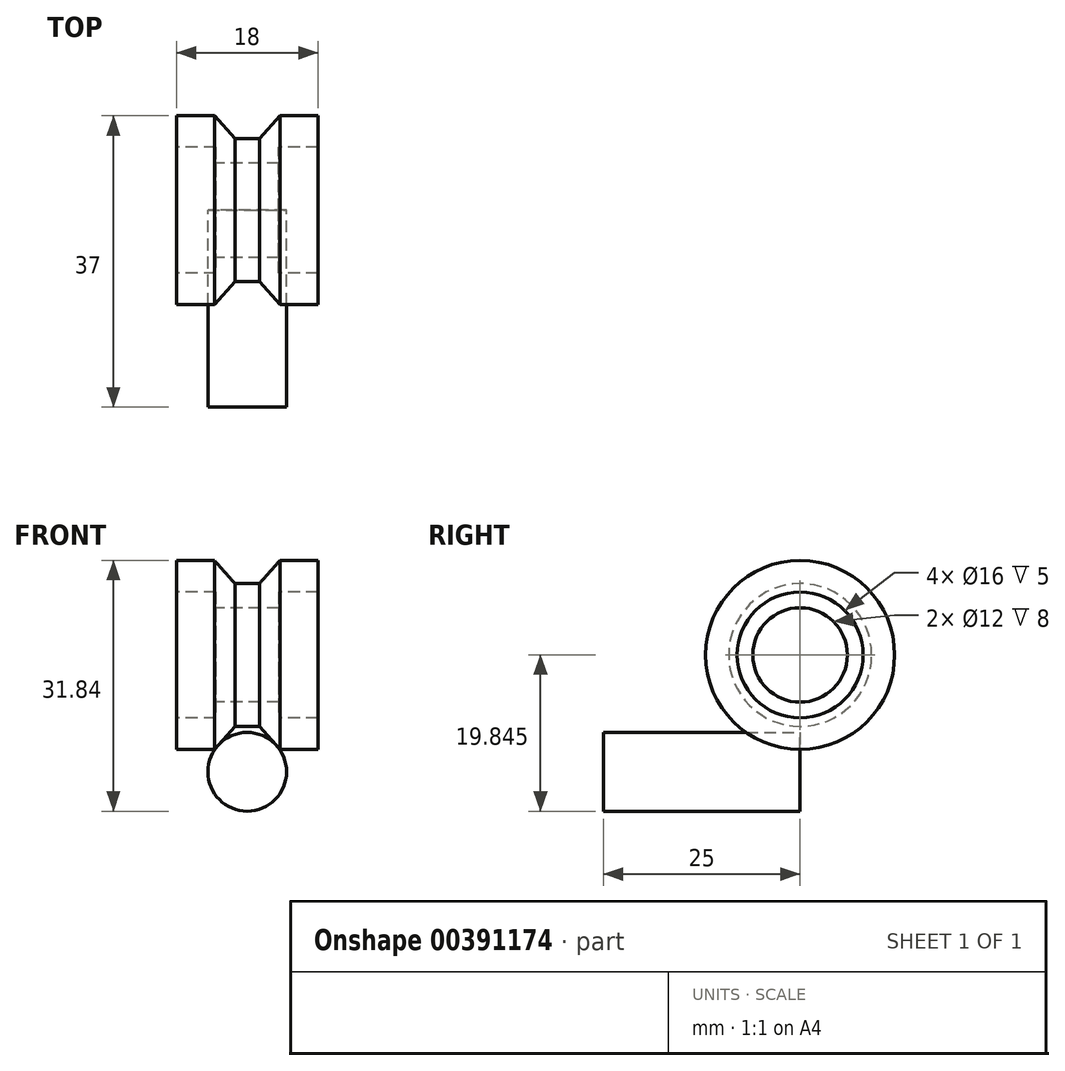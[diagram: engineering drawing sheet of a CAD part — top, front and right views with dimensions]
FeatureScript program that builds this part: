
annotation { "Feature Type Name" : "Feature", "Feature Type Description" : "" }
export const myFeature = defineFeature(function(context is Context, id is Id, definition is map)
    precondition{}
    {
        {
            var Q0;
            Q0=qCreatedBy(makeId("Front.planeOp"),FACE);
            var sketch = newSketch(context, id + "F0", { "sketchPlane" : qUnion([Q0])});
            skCircle(sketch, "E0", {"center": v(0, 0) * mm, "radius": 5 * mm});
            skSolve(sketch);
        }
        {
            var Q0;
            Q0=makeQuery(id+"F0.imprint","IMPRINT",FACE,{"disambiguationData":[TD([[makeQuery(id+"F0.imprint","IMPRINT",EDGE,{"derivedFrom":sQuery(id+"F0.wireOp",EDGE,"E0")}),1.0]])]});
            extrude(context, id + "F1", {"entities" : qUnion([Q0]), "depth" : 25 * mm});
        }
        {
            var Q0;
            Q0=qCreatedBy(makeId("Front.planeOp"),FACE);
            var sketch = newSketch(context, id + "F2", { "sketchPlane" : qUnion([Q0])});
            skLineSegment(sketch, "E1", {"start": v(-4.16, 2.84) * mm, "end": v(-1.56, 5.77) * mm});
            skPoint(sketch, "E2.startSnap0", {"position": v(-3.54, 3.54) * mm});
            skLineSegment(sketch, "E3", {"start": v(-9, 6.84) * mm, "end": v(-9, 2.84) * mm});
            skLineSegment(sketch, "E4", {"start": v(-4.16, 2.84) * mm, "end": v(-9, 2.84) * mm});
            skLineSegment(sketch, "E5.MirrorCS", {"start": v(9, 6.84) * mm, "end": v(9, 2.84) * mm});
            skLineSegment(sketch, "E6.MirrorCS", {"start": v(4.16, 2.84) * mm, "end": v(9, 2.84) * mm});
            skLineSegment(sketch, "E7.MirrorCS", {"start": v(4.16, 2.84) * mm, "end": v(1.56, 5.77) * mm});
            skPoint(sketch, "E8.MirrorP", {"position": v(3.54, 3.54) * mm});
            skLineSegment(sketch, "E9", {"start": v(-9, 6.84) * mm, "end": v(-4, 6.84) * mm});
            skLineSegment(sketch, "E10", {"start": v(9, 6.84) * mm, "end": v(4, 6.84) * mm});
            skLineSegment(sketch, "E11", {"start": v(4, 6.84) * mm, "end": v(4, 8.84) * mm});
            skLineSegment(sketch, "E12", {"start": v(-4, 6.84) * mm, "end": v(-4, 8.84) * mm});
            skLineSegment(sketch, "E13", {"start": v(-4, 14.84) * mm, "end": v(4, 14.84) * mm, "construction": true});
            skLineSegment(sketch, "E14", {"start": v(-1.56, 5.77) * mm, "end": v(1.56, 5.77) * mm});
            skPoint(sketch, "E15.orphan", {"position": v(0, 7.54) * mm});
            skLineSegment(sketch, "E16", {"start": v(-4, 8.84) * mm, "end": v(4, 8.84) * mm});
            skPoint(sketch, "E17.orphan", {"position": v(-4, 14.84) * mm});
            skPoint(sketch, "E18.orphan", {"position": v(4, 14.84) * mm});
            skPoint(sketch, "E19.MirrorP", {"position": v(0, 22.15) * mm});
            skLineSegment(sketch, "E20.MirrorCS", {"start": v(4, 22.84) * mm, "end": v(4, 20.84) * mm});
            skLineSegment(sketch, "E21.MirrorCS", {"start": v(-4, 22.84) * mm, "end": v(-4, 20.84) * mm});
            skPoint(sketch, "E22.MirrorP", {"position": v(3.54, 26.15) * mm});
            skLineSegment(sketch, "E23.MirrorCS", {"start": v(9, 22.84) * mm, "end": v(4, 22.84) * mm});
            skPoint(sketch, "E24.MirrorP", {"position": v(-3.54, 26.15) * mm});
            skLineSegment(sketch, "E25.MirrorCS", {"start": v(9, 22.84) * mm, "end": v(9, 26.84) * mm});
            skLineSegment(sketch, "E26.MirrorCS", {"start": v(4.16, 26.84) * mm, "end": v(9, 26.84) * mm});
            skLineSegment(sketch, "E27.MirrorCS", {"start": v(-9, 22.84) * mm, "end": v(-4, 22.84) * mm});
            skLineSegment(sketch, "E28.MirrorCS", {"start": v(4.16, 26.84) * mm, "end": v(1.56, 23.92) * mm});
            skLineSegment(sketch, "E29.MirrorCS", {"start": v(-4, 20.84) * mm, "end": v(4, 20.84) * mm});
            skLineSegment(sketch, "E30.MirrorCS", {"start": v(-9, 22.84) * mm, "end": v(-9, 26.84) * mm});
            skLineSegment(sketch, "E31.MirrorCS", {"start": v(-1.56, 23.92) * mm, "end": v(1.56, 23.92) * mm});
            skLineSegment(sketch, "E32.MirrorCS", {"start": v(-4.16, 26.84) * mm, "end": v(-9, 26.84) * mm});
            skLineSegment(sketch, "E33.MirrorCS", {"start": v(-4.16, 26.84) * mm, "end": v(-1.56, 23.92) * mm});
            skLineSegment(sketch, "E34", {"start": v(-4, 20.84) * mm, "end": v(-4, 8.84) * mm});
            skLineSegment(sketch, "E35", {"start": v(3.97, 20.67) * mm, "end": v(4, 8.84) * mm});
            skSolve(sketch);
        }
        {
            var Q0;
            Q0=makeQuery(id+"F2.imprint","IMPRINT",FACE,{"disambiguationData":[TD([[makeQuery(id+"F2.imprint","IMPRINT",EDGE,{"derivedFrom":sQuery(id+"F2.wireOp",EDGE,"E20.MirrorCS")}),-1.0]])]});
            var Q1;
            Q1=makeQuery(id+"F2.imprint","IMPRINT",FACE,{"disambiguationData":[TD([[makeQuery(id+"F2.imprint","IMPRINT",EDGE,{"derivedFrom":sQuery(id+"F2.wireOp",EDGE,"E1")}),1.0]])]});
            var Q2;
            Q2=sQuery(id+"F2.wireOp",EDGE,"E13");
            revolve(context, id + "F3", {"entities" : qUnion([Q0, Q1]), "axis" : qUnion([Q2]), "revolveType" : RevolveType.FULL});
        }
    });
